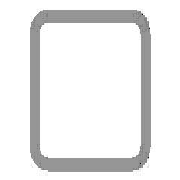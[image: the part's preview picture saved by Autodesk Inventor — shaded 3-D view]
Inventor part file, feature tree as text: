
AUTODESK INVENTOR PART (.ipt)
format: ipt  version: 2024 (Build 280153000, 153)  size: 137,216 bytes
history: native  units: mm (DEFAULTED — no unit token found)
features: other x4, plane x3, split x2, extrude x1, sketch x1
ambient origin geometry x8: Origin, YZ Plane, XZ Plane, XY Plane, X Axis, Y Axis, Z Axis, Center Point
bodies: Solid1 (feature_tree)
feature tree (11):
  parser-record x1  (decoder bookkeeping rows leaked as tree rows — omitted from the tree; the rows remain in map.json)
  other  "Driven Length"
  other  "Plano inicial"
  other  "Plano final"
  extrude  "Cuerpo"  TaperAngle=0.0deg  [1 undecoded]
  plane  "Plano de trabajo4"
  split  "Dividir1"
  plane  "Plano de trabajo5"
  split  "Dividir2"
  sketch  "Sketch3"  dims[d3=849.2mm d4=0.0mm d10=50.8mm d11=50.8mm d12=3.175mm d13=25.4mm d14=874.6mm d15=25.4mm d16=25.4mm d17=6.35mm d18=90.0deg d19=849.2mm]
  plane  "Work Plane3"
note: 1 required parameter value undecoded (feature->parameter linkage not recoverable at this tier; creation-order binding heuristic only, values carry confidence <= 0.55)
